# Revit family: 26344 Зарядное устройство и точка доступа Wi-Fi «Валли» 2xUSB и 1x220V Хоббика
name_source: partatom
category: Антураж
revit_build: Autodesk Revit 2018 (Build: 20180423_1000(x64)
units: mm (PartAtom-declared; Revit-internal decimal feet)

## family parameters
Всегда вертикально = Да
Источник визуального образа = Геометрия семейства
На основе рабочей плоскости = Нет
Общий = Нет
При загрузке вырезать с полостями = Нет
Точка расчета площади = Нет

## types (1)
- Зарядное устройство и точка доступа Wi-Fi «Валли» 2xUSB и 1x220V
    URL = https://hobbyka.ru
    Артикул товара = Арт. 26344
    Высота = 68 мм
    Группа модели = Умная городская мебель
    Длина = 180 мм
    Изготовитель = ООО «Хоббика»
    Изображение типоразмера = Зарядное устройство и точка доступа Wi-Fi «Валли» 2xUSB и 1x220V Арт 26344.jpg
    Материал изделия = Сталь
    Описание = Зарядное устройство и точка доступа Wi-Fi «Валли» 2xUSB и 1x220V
    Цвет каркаса = Серый
    Цвет отделки = Оранжевый
    Ширина = 160 мм
